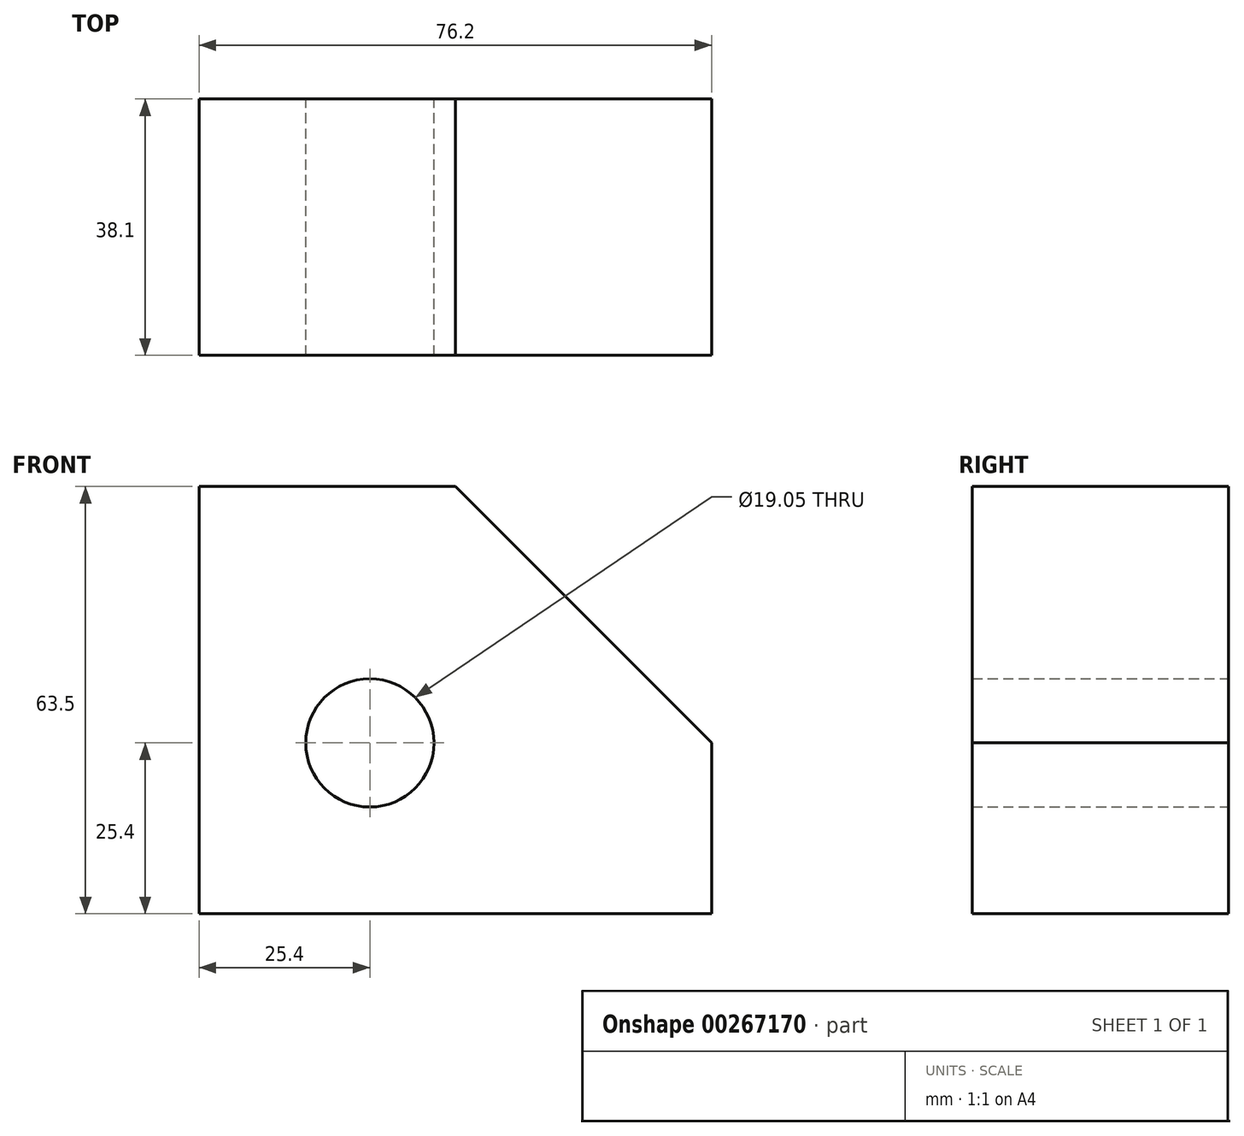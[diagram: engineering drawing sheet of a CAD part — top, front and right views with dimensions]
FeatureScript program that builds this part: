
annotation { "Feature Type Name" : "Feature", "Feature Type Description" : "" }
export const myFeature = defineFeature(function(context is Context, id is Id, definition is map)
    precondition{}
    {
        {
            var Q0;
            Q0=qCreatedBy(makeId("Front.planeOp"),FACE);
            var sketch = newSketch(context, id + "F0", { "sketchPlane" : qUnion([Q0])});
            skLineSegment(sketch, "E0", {"start": v(0, 0) * mm, "end": v(76.2, 0) * mm});
            skLineSegment(sketch, "E1", {"start": v(76.2, 0) * mm, "end": v(76.2, 25.4) * mm});
            skLineSegment(sketch, "E2", {"start": v(76.2, 25.4) * mm, "end": v(38.1, 63.5) * mm});
            skLineSegment(sketch, "E3", {"start": v(38.1, 63.5) * mm, "end": v(0, 63.5) * mm});
            skLineSegment(sketch, "E4", {"start": v(0, 63.5) * mm, "end": v(0, 0) * mm});
            skCircle(sketch, "E5", {"center": v(25.4, 25.4) * mm, "radius": 9.53 * mm});
            skSolve(sketch);
        }
        {
            var Q0;
            Q0=makeQuery(id+"F0.imprint","IMPRINT",FACE,{"disambiguationData":[TD([[makeQuery(id+"F0.imprint","IMPRINT",EDGE,{"derivedFrom":sQuery(id+"F0.wireOp",EDGE,"E0")}),1.0]])]});
            extrude(context, id + "F1", {"entities" : qUnion([Q0]), "depth" : 38.1 * mm, "symmetric" : true});
        }
    });
